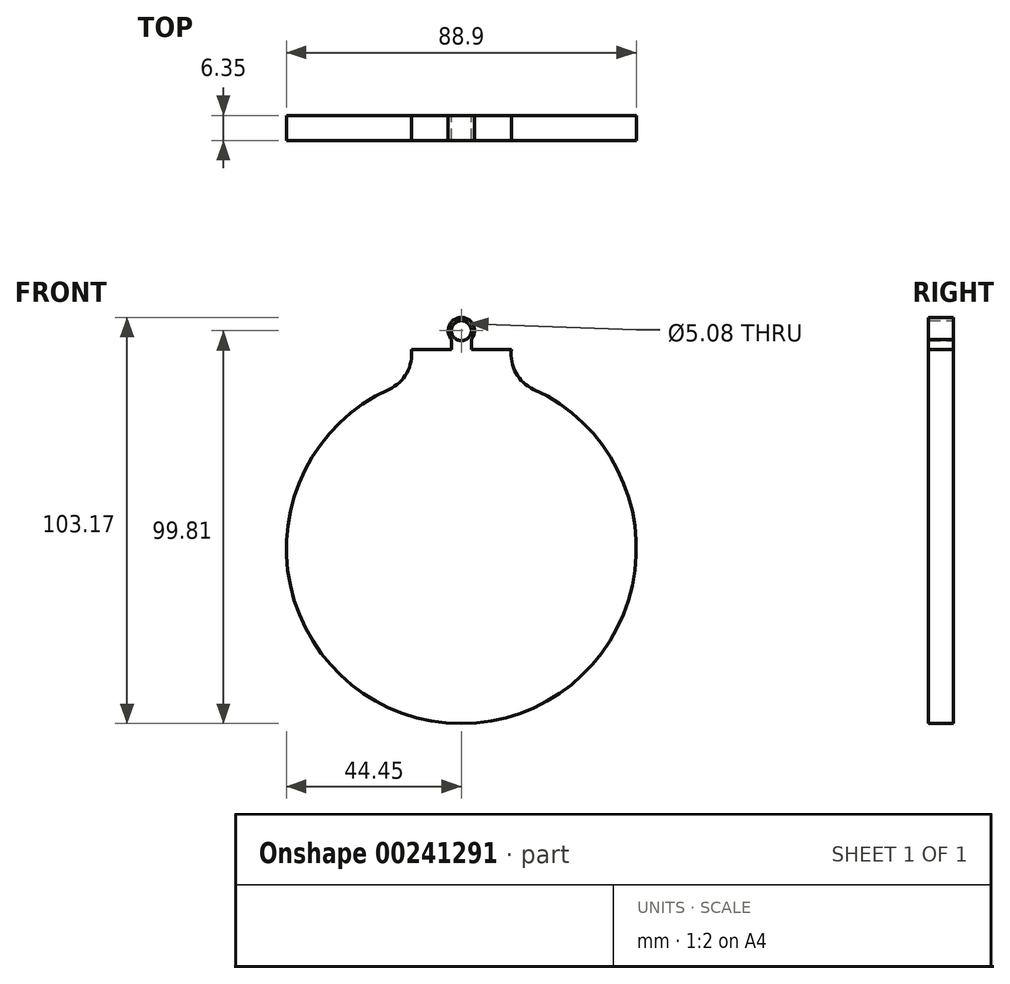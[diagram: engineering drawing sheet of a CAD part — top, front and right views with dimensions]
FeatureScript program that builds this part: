
annotation { "Feature Type Name" : "Feature", "Feature Type Description" : "" }
export const myFeature = defineFeature(function(context is Context, id is Id, definition is map)
    precondition{}
    {
        {
            var Q0;
            Q0=qCreatedBy(makeId("Front.planeOp"),FACE);
            var sketch = newSketch(context, id + "F0", { "sketchPlane" : qUnion([Q0])});
            skCircle(sketch, "E0", {"center": v(0, 0) * mm, "radius": 44.45 * mm});
            skLineSegment(sketch, "E1", {"start": v(0, 50.62) * mm, "end": v(-12.7, 50.62) * mm});
            skLineSegment(sketch, "E2", {"start": v(0, 50.62) * mm, "end": v(12.7, 50.62) * mm});
            skArc(sketch, "E3", {"start": v(-18.36, 40.48) * mm, "mid": v(-13.86, 44.62) * mm, "end": v(-12.7, 50.62) * mm});
            skArc(sketch, "E4", {"start": v(12.7, 50.62) * mm, "mid": v(13.86, 44.62) * mm, "end": v(18.36, 40.48) * mm});
            skLineSegment(sketch, "E5", {"start": v(2.54, 50.62) * mm, "end": v(2.54, 53.16) * mm});
            skLineSegment(sketch, "E6", {"start": v(-2.54, 50.62) * mm, "end": v(-2.54, 53.16) * mm});
            skCircle(sketch, "E7", {"center": v(0, 55.36) * mm, "radius": 3.36 * mm});
            skCircle(sketch, "E8", {"center": v(0, 55.36) * mm, "radius": 2.54 * mm});
            skSolve(sketch);
        }
        {
            var Q0;
            {var subQ0=sQuery(id+"F0.wireOp",EDGE,"E0");var subQ1=makeQuery(id+"F0.imprint","INTERSECT",VERTEX,{"derivedFrom":[subQ0,sQuery(id+"F0.wireOp",EDGE,"E3")]});Q0=makeQuery(id+"F0.imprint","IMPRINT",FACE,{"disambiguationData":[TD([[makeQuery(id+"F0.imprint","IMPRINT",EDGE,{"disambiguationData":[TD([[subQ1,1.0]])],"derivedFrom":subQ0}),1.0]])]});}
            var Q1;
            {var subQ4=sQuery(id+"F0.wireOp",EDGE,"E3");Q1=makeQuery(id+"F0.imprint","IMPRINT",FACE,{"disambiguationData":[TD([[makeQuery(id+"F0.imprint","IMPRINT",EDGE,{"derivedFrom":subQ4}),-1.0]])]});}
            var Q2;
            {var subQ0=sQuery(id+"F0.wireOp",EDGE,"E5");Q2=makeQuery(id+"F0.imprint","IMPRINT",FACE,{"disambiguationData":[TD([[makeQuery(id+"F0.imprint","IMPRINT",EDGE,{"derivedFrom":subQ0}),1.0]])]});}
            var Q3;
            Q3=makeQuery(id+"F0.imprint","IMPRINT",FACE,{"disambiguationData":[TD([[makeQuery(id+"F0.imprint","IMPRINT",EDGE,{"derivedFrom":sQuery(id+"F0.wireOp",EDGE,"E8")}),-1.0]])]});
            extrude(context, id + "F1", {"entities" : qUnion([Q0, Q1, Q2, Q3]), "depth" : 6.35 * mm});
        }
    });
